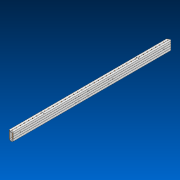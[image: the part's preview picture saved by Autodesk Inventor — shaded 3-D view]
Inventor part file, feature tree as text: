
AUTODESK INVENTOR PART (.ipt)
format: ipt  version: 2022.2 (Build 262287000, 287)  size: 714,752 bytes
history: native  units: in
note: dims shown in document units (in); Inventor stores cm internally (conversion verified against a paired STEP export)
features: other x51, reference x14, sketch x6, extrude x5, pattern_linear x1, hole x1
ambient origin geometry x8: Origin, YZ Plane, XZ Plane, XY Plane, X Axis, Y Axis, Z Axis, Center Point
bodies: Solid1 (feature_tree)
feature tree (78):
  extrude  "Extrusion1"  Depth=2.0in
  other  "Work Axis1"
  pattern_linear  "Rectangular Pattern1"  Count1=39  [1 undecoded]
  extrude  "Extrusion2"  Depth=1.0in
  extrude  "Extrusion3"  Depth=1.0in
  extrude  "Extrusion4"  Depth=1.0in
  hole  "Hole1"  [1 undecoded]
  extrude  "Extrusion5"  TaperAngle=0.0deg  [1 undecoded]
  sketch  "Sketch1"  dims[d0=1.0in d1=2.0in]
  other  "Work Axis2"
  other  "Work Axis3"
  other  "Work Axis4"
  other  "Work Axis5"
  other  "Work Axis6"
  other  "Work Axis7"
  other  "Work Axis8"
  other  "Work Axis9"
  other  "Work Axis10"
  other  "Work Axis60"
  other  "Work Axis61"
  other  "Work Axis62"
  other  "Work Axis63"
  other  "Work Axis64"
  other  "Work Axis65"
  other  "Work Axis66"
  other  "Work Axis67"
  other  "Work Axis68"
  other  "Work Axis69"
  other  "Work Axis70"
  other  "Work Axis71"
  other  "Work Axis72"
  other  "Work Axis73"
  other  "Work Axis74"
  other  "Work Axis75"
  other  "Work Axis76"
  other  "Work Axis77"
  other  "Work Axis78"
  other  "Work Axis79"
  other  "Work Axis80"
  other  "Work Axis81"
  other  "Work Axis82"
  other  "Work Axis83"
  other  "Work Axis84"
  other  "Work Axis85"
  other  "Work Axis86"
  other  "Work Axis87"
  other  "Work Axis88"
  sketch  "Sketch3"  dims[d2=20.0in]
  sketch  "Sketch4"  dims[d3=0.0in d4=15.3543in]
  reference  "Reference1"
  reference  "Reference2"
  reference  "Reference3"
  reference  "Reference4"
  reference  "Reference5"
  reference  "Reference6"
  reference  "Reference7"
  reference  "Reference8"
  sketch  "Sketch5"  dims[d6=1.0in d8=0.17in]
  reference  "Reference9"
  reference  "Reference10"
  reference  "Reference11"
  reference  "Reference12"
  sketch  "Sketch6"  dims[d9=0.0in d10=0.0in d11=1.0in]
  sketch  "Sketch7"  dims[d12=2.2325in d13=6.0in d14=0.0in d15=0.0in d16=0.0in d17=0.0in d18=1.0in d19=1.5in d20=0.17in d21=0.2362in d22=0.1575in d23=0.0787in d24=90.0deg d25=0.315in d26=0.8108in d27=0.0in d28=0.0in]
  reference  "Reference13"
  reference  "Reference14"
  other  "Cut-Extrude2"
  parser-record x2  (decoder bookkeeping rows leaked as tree rows — omitted from the tree; the rows remain in map.json)
  other  "Chassis.iam"
  other  "VersaFrame 45 Degree Gusset (217-3552):12"
  other  "VersaFrame 45 Degree Gusset (217-3552):9"
  other  "VersaFrame 135 Degree Gusset Modifed 2(217-3556):5"
  other  "VersaFrame 135 Degree Gusset Modifed 2(217-3556):7"
  other  "Robot.iam"
  other  "Tower:1"
  other  "1 x 1 x 0.040 x 26 Tower Stablizer Pre-Drilled VersaFrame Aluminum Tube Stock Cut (217-3426):3"
  other  "1 x 1 x 0.040 x 26 Tower Stablizer Pre-Drilled VersaFrame Aluminum Tube Stock Cut (217-3426):4"
note: 3 required parameter values undecoded (feature->parameter linkage not recoverable at this tier; creation-order binding heuristic only, values carry confidence <= 0.55)
note: 2 file-system paths scrubbed to <path> (originals preserved in map.json)
